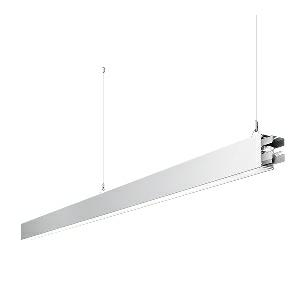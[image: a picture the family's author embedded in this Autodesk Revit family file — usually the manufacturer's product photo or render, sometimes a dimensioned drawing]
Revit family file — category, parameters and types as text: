
# Revit family: idoo_line_-_ilp_6000_vtl_d_mid_00806458_24d3
name_source: partatom
category: Lighting Fixtures
units: mm (PartAtom-declared; Revit-internal decimal feet)

## family parameters
Cut with Voids When Loaded = No
Host = Face
Light Source = No
Part Type = Normal
Room Calculation Point = No
Round Connector Dimension = Use Diameter
Shared = No

## types (1)
- IDOO.line - ILP 6000/VTL/D MID (1 x LED, 6150 lm, 2700-6500K)
    Apparent Load = 63 VA
    Approval mark = CE
    CIE Flux Codes = 66 91 98 40 100
    Color Rendering = 90-100
    Color Temperature = 2700-6500K
    Control Gear = Electronic ballast
    Default Elevation = 1800 mm
    Description = ILP 6000/VTL/D|Suspended luminaire|light source: LED|connected load: 220-240 V, 50/60 Hz|Power consumption: approx. 63 W|standby: approx. 0,25|luminous flux: 6150 lm|luminous efficacy: 97 lm/W|light distribution: Direct/indirect|direct ratio: approx. 40 %|colour temperature: Cold white, ca. 2700-6500 K|color rendering index (CRI): >= 90|chromaticity tolerance:  3 SDCM|System of protection: IP 40|technology: Continuously dimmable|luminaire body|material: Sectional aluminium|colour: White|lamp cover: Acrylic (PMMA), Clear|mains lead: 1,0 m With free stranded wires|Fastening: Steel cable 0.3 - 0.7 m|glare control: Prism aperture|luminance(L65): <= 2700 cd/m|unified glare rating(4H 8H): <=  16|special features: Specified values at approx. 4000 K, DALI Load 1x, Through-wired, up to 18 m on one mains connection, External control required for Dali Device type 8, Flicker-free, Constant luminous flux between 2700 and 6500 K, Constant colour temperature over the whole dimming range, Suitable as emergency lighting, Mechanical and electrical connection of the individual modules without tools|
    Frequency = 50 Hz
    Height = 110 mm
    Lamp = 1 x LED
    Lamp Light Flux = 6150 lm
    Lamp count = 1
    Length = 2244 mm
    Luminous efficacy = 98 lm/W
    Manufacturer = Waldmann
    ModVariant = No
    Model = 00806458
    Mounting Place = Ceiling
    Mounting Type = Pendant
    Number of Poles = 1
    OnlyDefault = Yes
    Power Factor = 1
    Product Name = IDOO.line - ILP 6000/VTL/D MID
    Product group = Suspended luminaire
    ProductGroupID = 9
    Protection Class = Protection class I
    Protection Degree = IP 40
    RLX_Detail_Level = 1
    RLX_Emergency_Light_Flux = 0 lm
    RLX_Emergency_Type = 0
    RLX_Emergency_Type_DB = No
    RlxData = <blob elided: 22489 chars, md5=808d7a75>
    Socket = socket
    Standby Power = 0 W
    System Light Flux = 6150 lm
    System Power = 63 W
    Type Comments = Product without accessories
    Type Image = 113314000-00692606.jpg
    URL = http://relux.com
    VarID = ---
    Voltage = 230 V
    Voltage Range = 220-240 V
    Weight = 0.00 kg
    Width = 60 mm

## geometry (parser evidence)
native form markers: Blend x4, Sweep x14
no freeform markers — native parametric forms only
